# Revit family: Accessory-Towel_Bar-KOHLER-Square-K-23285
name_source: partatom
category: Specialty Equipment
units: mm (PartAtom-declared; Revit-internal decimal feet)

## family parameters
Cut with Voids When Loaded = No
Host = Face
OmniClass Number = 23.31.25.25
OmniClass Title = Towel Bars
Part Type = Normal
Room Calculation Point = No
Round Connector Dimension = Use Diameter
Shared = No

## types (1)
- RGD-Polished Rose Gold
    ADA Compliant = No
    Assembly Code = C1030200
    Date Modified = 06/09/2023
    Default Elevation = 42"
    Description = 24 Inch towel bar
    Finish = Kohler-Metal-RGD-Polished_Rose_Gold
    Height = 2"
    Length = 26"
    Manufacturer = Kohler Co.
    Master Format 2014 = 10 28 00
    Master Format 2014 Name = Toilet, Bath, and Laundry Accessories
    Material = Premium Metal Construction
    Model = K-23285M-RGD
    Product Name = Square
    Type = 1
    URL = https://la.kohler.com
    WaterSense Certified = No
    Width = 3 1/16"

## geometry (parser evidence)
native form markers: Sweep x5
no freeform markers — native parametric forms only
